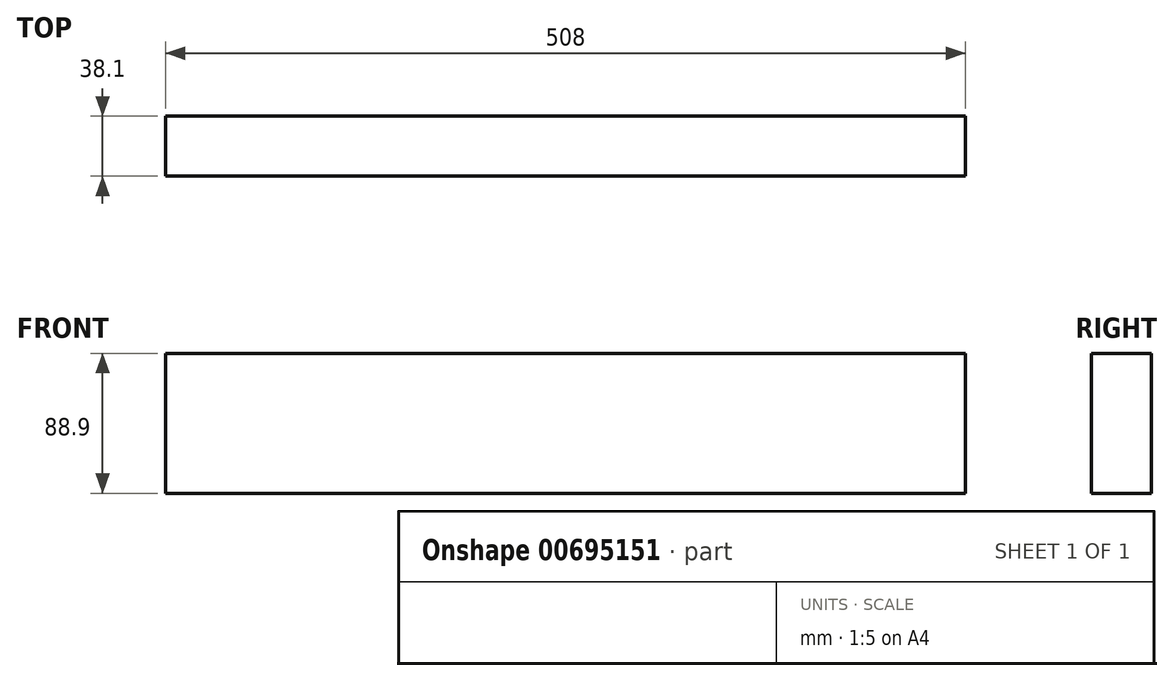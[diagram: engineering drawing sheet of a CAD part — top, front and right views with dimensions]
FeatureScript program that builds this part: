
annotation { "Feature Type Name" : "Feature", "Feature Type Description" : "" }
export const myFeature = defineFeature(function(context is Context, id is Id, definition is map)
    precondition{}
    {
        {
            var Q0;
            Q0=qCreatedBy(makeId("Right.planeOp"),FACE);
            var sketch = newSketch(context, id + "F0", { "sketchPlane" : qUnion([Q0])});
            skLineSegment(sketch, "E0.bottom", {"start": v(-356.84, -1084.59) * mm, "end": v(-318.74, -1084.59) * mm});
            skLineSegment(sketch, "E0.top", {"start": v(-356.84, -1173.49) * mm, "end": v(-318.74, -1173.49) * mm});
            skLineSegment(sketch, "E0.left", {"start": v(-356.84, -1084.59) * mm, "end": v(-356.84, -1173.49) * mm});
            skLineSegment(sketch, "E0.right", {"start": v(-318.74, -1084.59) * mm, "end": v(-318.74, -1173.49) * mm});
            skSolve(sketch);
        }
        {
            var Q0;
            Q0 = qSketchRegion(id + "F0", true);
            extrude(context, id + "F1", {"entities" : qUnion([Q0]), "depth" : 508 * mm, "offsetDistance" : 25.4 * mm});
        }
    });
